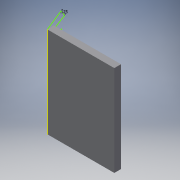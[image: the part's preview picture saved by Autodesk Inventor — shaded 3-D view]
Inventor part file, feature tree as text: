
AUTODESK INVENTOR PART (.ipt)
format: ipt  version: 2017 (Build 210142000, 142)  size: 108,032 bytes
history: native  units: in
note: dims shown in document units (in); Inventor stores cm internally (conversion verified against a paired STEP export)
features: extrude x2, sketch x2, fillet x1
ambient origin geometry x8: Origin, YZ Plane, XZ Plane, XY Plane, X Axis, Y Axis, Z Axis, Center Point
bodies: Solid1 (feature_tree)
feature tree (5):
  extrude  "Extrusion1"  Depth=0.125in TaperAngle=0.0deg
  extrude  "Extrusion2"  Depth=1.25in TaperAngle=0.0deg
  fillet  "Fillet1"  Radius=0.25in
  sketch  "Sketch1"  dims[d0=1.25in d1=0.125in d2=0.0in]
  sketch  "Sketch2"  dims[d3=0.125in d4=1.25in d5=0.0in d6=0.25in]
